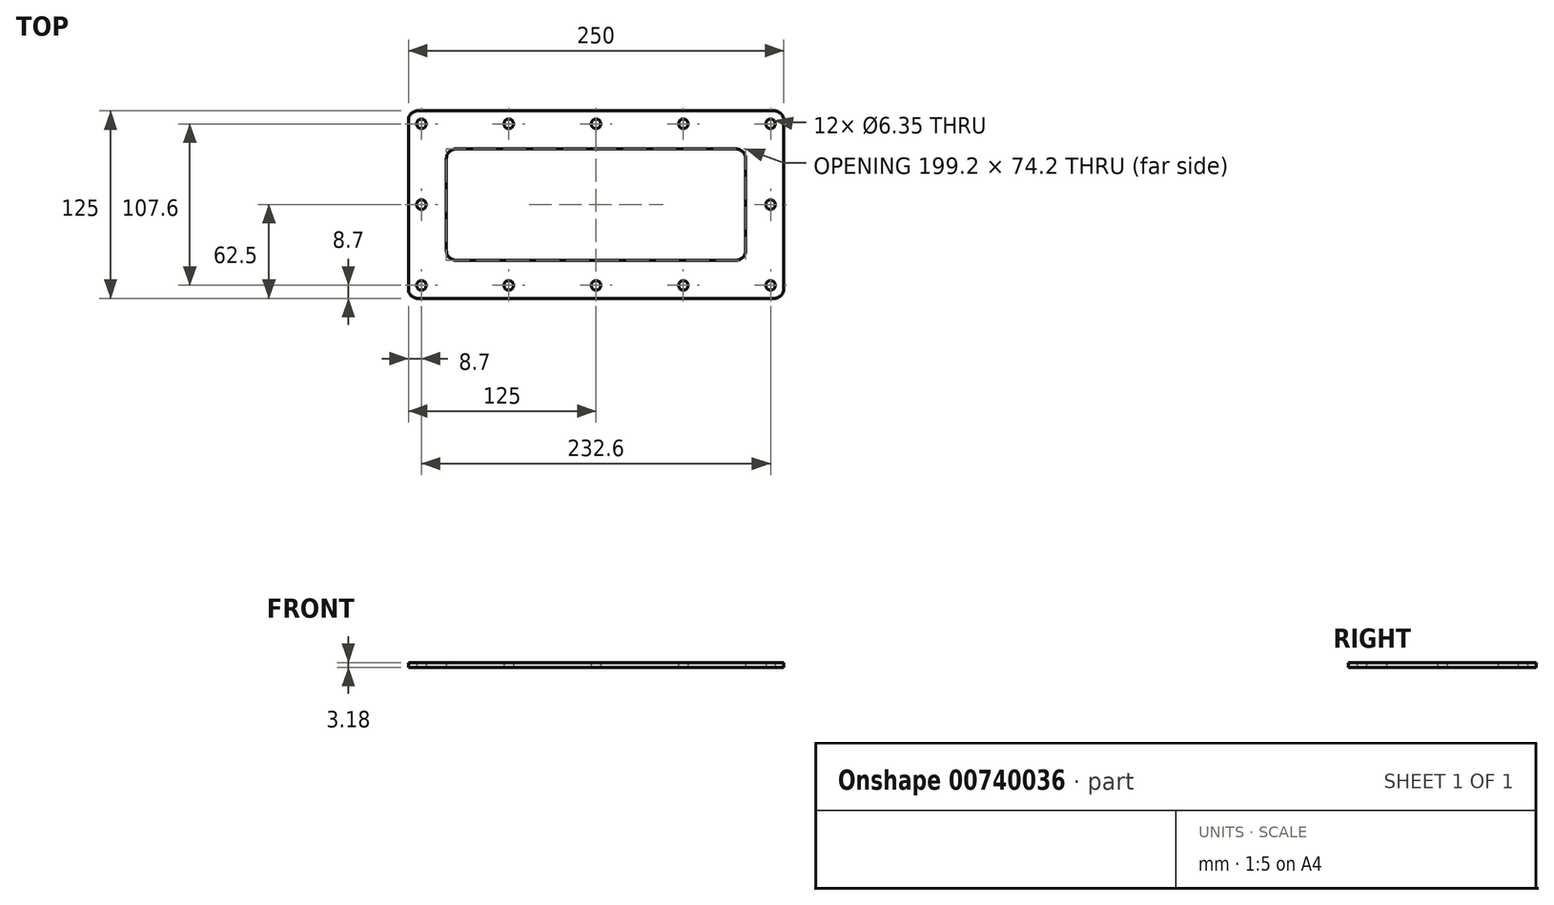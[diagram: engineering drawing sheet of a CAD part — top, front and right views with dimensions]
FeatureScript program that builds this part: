
annotation { "Feature Type Name" : "Feature", "Feature Type Description" : "" }
export const myFeature = defineFeature(function(context is Context, id is Id, definition is map)
    precondition{}
    {
        {
            var Q0;
            Q0=qCreatedBy(makeId("Top.planeOp"),FACE);
            var sketch = newSketch(context, id + "F0", { "sketchPlane" : qUnion([Q0])});
            skLineSegment(sketch, "E0.bottom", {"start": v(-118.65, 62.5) * mm, "end": v(118.65, 62.5) * mm});
            skLineSegment(sketch, "E0.top", {"start": v(-118.65, -62.5) * mm, "end": v(118.65, -62.5) * mm});
            skLineSegment(sketch, "E0.left", {"start": v(-125, 56.15) * mm, "end": v(-125, -56.15) * mm});
            skLineSegment(sketch, "E0.right", {"start": v(125, 56.15) * mm, "end": v(125, -56.15) * mm});
            skPoint(sketch, "E0.middle", {"position": v(0, 0) * mm});
            skLineSegment(sketch, "E1.bottom", {"start": v(-93.25, 37.1) * mm, "end": v(93.25, 37.1) * mm});
            skLineSegment(sketch, "E1.top", {"start": v(-93.25, -37.1) * mm, "end": v(93.25, -37.1) * mm});
            skLineSegment(sketch, "E1.left", {"start": v(-99.6, 30.75) * mm, "end": v(-99.6, -30.75) * mm});
            skLineSegment(sketch, "E1.right", {"start": v(99.6, 30.75) * mm, "end": v(99.6, -30.75) * mm});
            skPoint(sketch, "E2.visualSharp", {"position": v(-99.6, 37.1) * mm});
            skArc(sketch, "E2.filletArc", {"start": v(-93.25, 37.1) * mm, "mid": v(-97.74, 35.24) * mm, "end": v(-99.6, 30.75) * mm});
            skPoint(sketch, "E3.visualSharp", {"position": v(-99.6, -37.1) * mm});
            skArc(sketch, "E3.filletArc", {"start": v(-99.6, -30.75) * mm, "mid": v(-97.74, -35.24) * mm, "end": v(-93.25, -37.1) * mm});
            skPoint(sketch, "E4.visualSharp", {"position": v(99.6, -37.1) * mm});
            skArc(sketch, "E4.filletArc", {"start": v(93.25, -37.1) * mm, "mid": v(97.74, -35.24) * mm, "end": v(99.6, -30.75) * mm});
            skPoint(sketch, "E5.visualSharp", {"position": v(99.6, 37.1) * mm});
            skArc(sketch, "E5.filletArc", {"start": v(99.6, 30.75) * mm, "mid": v(97.74, 35.24) * mm, "end": v(93.25, 37.1) * mm});
            skPoint(sketch, "E6.visualSharp", {"position": v(125, 62.5) * mm});
            skArc(sketch, "E6.filletArc", {"start": v(125, 56.15) * mm, "mid": v(123.14, 60.64) * mm, "end": v(118.65, 62.5) * mm});
            skPoint(sketch, "E7.visualSharp", {"position": v(125, -62.5) * mm});
            skArc(sketch, "E7.filletArc", {"start": v(118.65, -62.5) * mm, "mid": v(123.14, -60.64) * mm, "end": v(125, -56.15) * mm});
            skPoint(sketch, "E8.visualSharp", {"position": v(-125, -62.5) * mm});
            skArc(sketch, "E8.filletArc", {"start": v(-125, -56.15) * mm, "mid": v(-123.14, -60.64) * mm, "end": v(-118.65, -62.5) * mm});
            skPoint(sketch, "E9.visualSharp", {"position": v(-125, 62.5) * mm});
            skArc(sketch, "E9.filletArc", {"start": v(-118.65, 62.5) * mm, "mid": v(-123.14, 60.64) * mm, "end": v(-125, 56.15) * mm});
            skCircle(sketch, "E10", {"center": v(-116.3, 53.8) * mm, "radius": 3.18 * mm});
            skCircle(sketch, "E11", {"center": v(-58.15, 53.8) * mm, "radius": 3.18 * mm});
            skCircle(sketch, "E12", {"center": v(0, 53.8) * mm, "radius": 3.18 * mm});
            skCircle(sketch, "E13", {"center": v(58.15, 53.8) * mm, "radius": 3.18 * mm});
            skCircle(sketch, "E14", {"center": v(-116.3, 0) * mm, "radius": 3.18 * mm});
            skCircle(sketch, "E15", {"center": v(-116.3, -53.8) * mm, "radius": 3.18 * mm});
            skCircle(sketch, "E16", {"center": v(116.3, 53.8) * mm, "radius": 3.18 * mm});
            skCircle(sketch, "E17.MirrorC", {"center": v(116.3, 0) * mm, "radius": 3.18 * mm});
            skCircle(sketch, "E18.MirrorC", {"center": v(116.3, -53.8) * mm, "radius": 3.18 * mm});
            skCircle(sketch, "E19.MirrorC", {"center": v(-58.15, -53.8) * mm, "radius": 3.18 * mm});
            skCircle(sketch, "E20.MirrorC", {"center": v(0, -53.8) * mm, "radius": 3.18 * mm});
            skCircle(sketch, "E21.MirrorC", {"center": v(58.15, -53.8) * mm, "radius": 3.18 * mm});
            skSolve(sketch);
        }
        {
            var Q0;
            Q0 = qSketchRegion(id + "F0", true);
            extrude(context, id + "F1", {"entities" : qUnion([Q0]), "depth" : 3.17 * mm, "offsetDistance" : 25.4 * mm});
        }
    });
